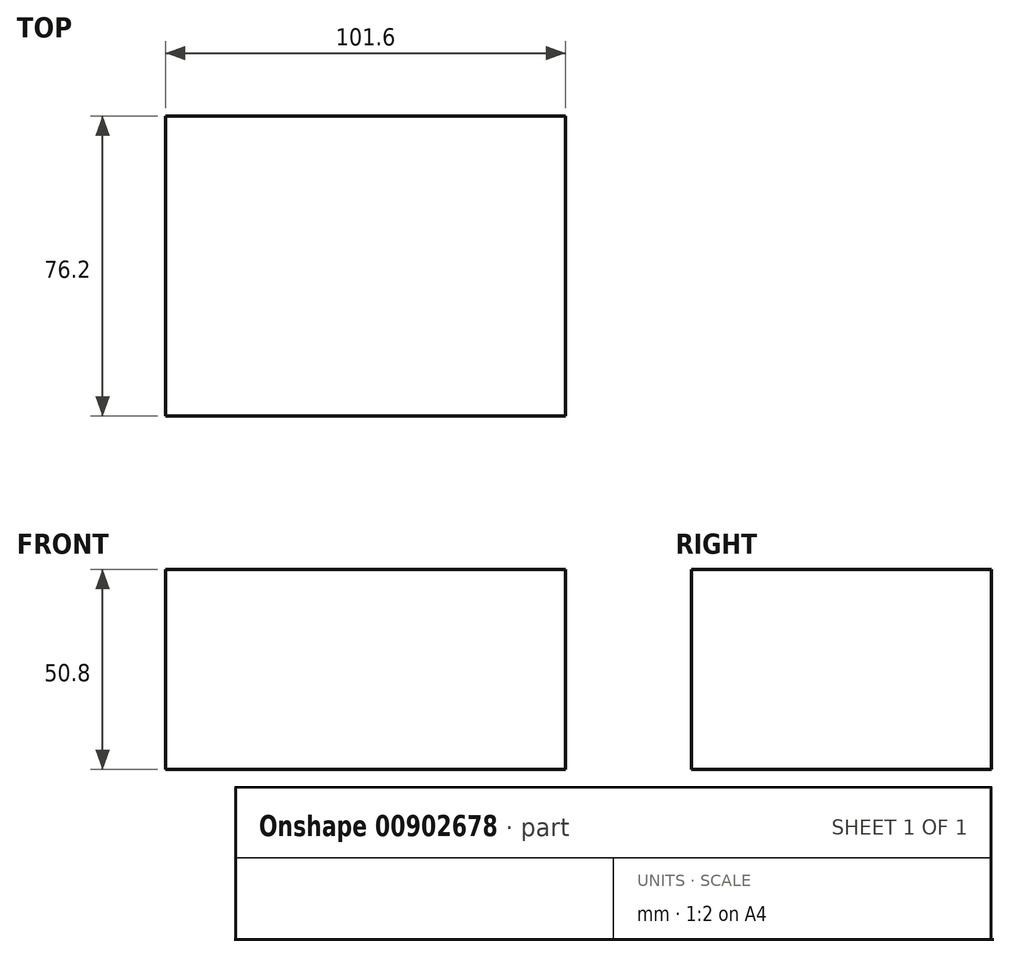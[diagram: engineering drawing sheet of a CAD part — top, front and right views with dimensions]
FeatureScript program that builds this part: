
annotation { "Feature Type Name" : "Feature", "Feature Type Description" : "" }
export const myFeature = defineFeature(function(context is Context, id is Id, definition is map)
    precondition{}
    {
        {
            var Q0;
            Q0=qCreatedBy(makeId("Top.planeOp"),FACE);
            var sketch = newSketch(context, id + "F0", { "sketchPlane" : qUnion([Q0])});
            skLineSegment(sketch, "E0.bottom", {"start": v(0, 0) * mm, "end": v(101.6, 0) * mm});
            skLineSegment(sketch, "E0.top", {"start": v(0, 76.2) * mm, "end": v(101.6, 76.2) * mm});
            skLineSegment(sketch, "E0.left", {"start": v(0, 0) * mm, "end": v(0, 76.2) * mm});
            skLineSegment(sketch, "E0.right", {"start": v(101.6, 0) * mm, "end": v(101.6, 76.2) * mm});
            skSolve(sketch);
        }
        {
            var Q0;
            Q0 = qSketchRegion(id + "F0", true);
            extrude(context, id + "F1", {"entities" : qUnion([Q0]), "depth" : 50.8 * mm, "offsetDistance" : 25.4 * mm});
        }
    });
